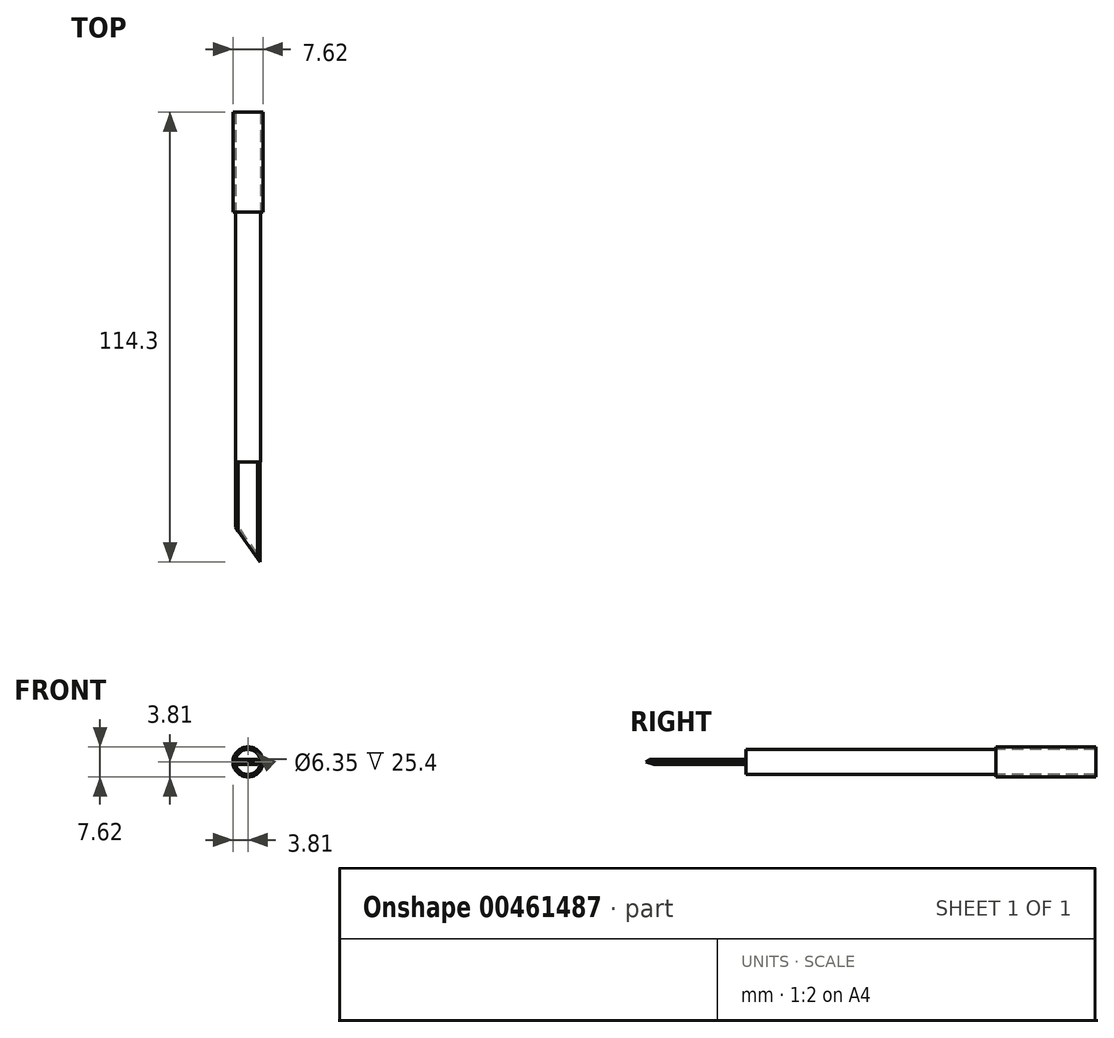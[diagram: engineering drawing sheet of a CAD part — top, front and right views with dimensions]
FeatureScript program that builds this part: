
annotation { "Feature Type Name" : "Feature", "Feature Type Description" : "" }
export const myFeature = defineFeature(function(context is Context, id is Id, definition is map)
    precondition{}
    {
        {
            var Q0;
            Q0=qCreatedBy(makeId("Front.planeOp"),FACE);
            var sketch = newSketch(context, id + "F0", { "sketchPlane" : qUnion([Q0])});
            skCircle(sketch, "E0", {"center": v(0, 0) * mm, "radius": 3.18 * mm});
            skSolve(sketch);
        }
        {
            var Q0;
            Q0=makeQuery(id+"F0.imprint","IMPRINT",FACE,{"disambiguationData":[TD([[makeQuery(id+"F0.imprint","IMPRINT",EDGE,{"derivedFrom":sQuery(id+"F0.wireOp",EDGE,"E0")}),1.0]])]});
            extrude(context, id + "F1", {"entities" : qUnion([Q0]), "depth" : 88.9 * mm});
        }
        {
            var Q0;
            Q0=makeQuery(id+"F1.opExtrude","CAP_FACE",FACE,{"disambiguationData":[OSD([sQuery(id+"F0.wireOp",EDGE,"E0")])],"isStart":false});
            var sketch = newSketch(context, id + "F2", { "sketchPlane" : qUnion([Q0])});
            skLineSegment(sketch, "E1", {"start": v(0, -3.18) * mm, "end": v(0, 0) * mm});
            skLineSegment(sketch, "E2", {"start": v(0, 0) * mm, "end": v(0, 3.18) * mm});
            skLineSegment(sketch, "E3.right", {"start": v(11.11, 0.64) * mm, "end": v(11.11, -0.64) * mm});
            skLineSegment(sketch, "E4", {"start": v(-1.59, 0.64) * mm, "end": v(-3.11, 0.64) * mm});
            skLineSegment(sketch, "E5", {"start": v(-3.11, 0.64) * mm, "end": v(3.11, 0.64) * mm});
            skLineSegment(sketch, "E6", {"start": v(-1.59, -0.64) * mm, "end": v(-3.11, -0.64) * mm});
            skLineSegment(sketch, "E7", {"start": v(-3.11, -0.64) * mm, "end": v(3.11, -0.64) * mm});
            skLineSegment(sketch, "E8.left", {"start": v(-3.11, 0.64) * mm, "end": v(-3.11, -0.64) * mm});
            skLineSegment(sketch, "E8.right", {"start": v(3.11, 0.64) * mm, "end": v(3.11, -0.64) * mm});
            skSolve(sketch);
        }
        {
            var Q0;
            {var subQ4=sQuery(id+"F2.wireOp",EDGE,"E8.left");Q0=makeQuery(id+"F2.imprint","IMPRINT",FACE,{"disambiguationData":[TD([[makeQuery(id+"F2.imprint","IMPRINT",EDGE,{"derivedFrom":subQ4}),1.0]])]});}
            var Q1;
            {var subQ0=sQuery(id+"F2.wireOp",EDGE,"E8.right");Q1=makeQuery(id+"F2.imprint","IMPRINT",FACE,{"disambiguationData":[TD([[makeQuery(id+"F2.imprint","IMPRINT",EDGE,{"derivedFrom":subQ0}),-1.0]])]});}
            extrude(context, id + "F3", {"entities" : qUnion([Q0, Q1]), "operationType" : NewBodyOperationType.ADD, "depth" : 25.4 * mm});
        }
        {
            var Q0;
            Q0=makeQuery(id+"F3.opExtrude","SWEPT_FACE",FACE,{"disambiguationData":[OSD([sQuery(id+"F2.wireOp",EDGE,"E5")])]});
            var sketch = newSketch(context, id + "F4", { "sketchPlane" : qUnion([Q0])});
            skLineSegment(sketch, "E9", {"start": v(3.11, -114.3) * mm, "end": v(-3.11, -105.48) * mm});
            skLineSegment(sketch, "E10", {"start": v(-3.11, -114.3) * mm, "end": v(3.11, -114.3) * mm});
            skSolve(sketch);
        }
        {
            var Q0;
            {var subQ0=sQuery(id+"F4.wireOp",EDGE,"E9");Q0=makeQuery(id+"F4.imprint","IMPRINT",FACE,{"disambiguationData":[TD([[makeQuery(id+"F4.imprint","IMPRINT",EDGE,{"derivedFrom":subQ0}),1.0]])]});}
            extrude(context, id + "F5", {"entities" : qUnion([Q0]), "operationType" : NewBodyOperationType.REMOVE, "oppositeDirection" : true, "depth" : 25.4 * mm});
        }
        {
            var Q0;
            Q0=makeQuery(id+"F3.opExtrude","SWEPT_EDGE",EDGE,{"disambiguationData":[OSD([sQuery(id+"F0.wireOp",EDGE,"E0"),sQuery(id+"F2.wireOp",EDGE,"E5"),sQuery(id+"F2.wireOp",EDGE,"E8.left")])]});
            var Q1;
            Q1=makeQuery(id+"F5.boolean.opBoolean","COPY",EDGE,{"derivedFrom":makeQuery(id+"F5.opExtrude","CAP_EDGE",EDGE,{"disambiguationData":[OSD([sQuery(id+"F4.wireOp",EDGE,"E9")])],"isStart":true})});
            var Q2;
            Q2=makeQuery(id+"F3.opExtrude","SWEPT_EDGE",EDGE,{"disambiguationData":[OSD([sQuery(id+"F0.wireOp",EDGE,"E0"),sQuery(id+"F2.wireOp",EDGE,"E5"),sQuery(id+"F2.wireOp",EDGE,"E8.right")])]});
            chamfer(context, id + "F6", {"entities" : qUnion([Q0, Q1, Q2]), "width" : 0.64 * mm, "tangentPropagation" : true});
        }
        {
            var Q0;
            Q0=makeQuery(id+"F5.boolean.opBoolean","INTERSECT",EDGE,{"derivedFrom":[makeQuery(id+"F3.opExtrude","SWEPT_FACE",FACE,{"disambiguationData":[OSD([sQuery(id+"F2.wireOp",EDGE,"E7")])]}),makeQuery(id+"F5.opExtrude","SWEPT_FACE",FACE,{"disambiguationData":[OSD([sQuery(id+"F4.wireOp",EDGE,"E9")])]})]});
            var Q1;
            Q1=makeQuery(id+"F3.opExtrude","SWEPT_EDGE",EDGE,{"disambiguationData":[OSD([sQuery(id+"F0.wireOp",EDGE,"E0"),sQuery(id+"F2.wireOp",EDGE,"E7"),sQuery(id+"F2.wireOp",EDGE,"E8.left")])]});
            var Q2;
            Q2=makeQuery(id+"F3.opExtrude","SWEPT_EDGE",EDGE,{"disambiguationData":[OSD([sQuery(id+"F0.wireOp",EDGE,"E0"),sQuery(id+"F2.wireOp",EDGE,"E7"),sQuery(id+"F2.wireOp",EDGE,"E8.right")])]});
            chamfer(context, id + "F7", {"entities" : qUnion([Q0, Q1, Q2]), "width" : 0.64 * mm, "tangentPropagation" : true});
        }
        {
            var Q0;
            Q0=makeQuery(id+"F1.opExtrude","CAP_FACE",FACE,{"disambiguationData":[OSD([sQuery(id+"F0.wireOp",EDGE,"E0")])],"isStart":true});
            extrude(context, id + "F8", {"entities" : qUnion([Q0]), "operationType" : NewBodyOperationType.REMOVE, "oppositeDirection" : true, "depth" : 25.4 * mm});
        }
        {
            var Q0;
            Q0=makeQuery(id+"F8.boolean.opBoolean","COPY",FACE,{"derivedFrom":makeQuery(id+"F8.opExtrude","CAP_FACE",FACE,{"disambiguationData":[OSD([sQuery(id+"F0.wireOp",EDGE,"E0")])],"isStart":false})});
            var sketch = newSketch(context, id + "F9", { "sketchPlane" : qUnion([Q0])});
            skCircle(sketch, "E11", {"center": v(0, 0) * mm, "radius": 3.81 * mm});
            skSolve(sketch);
        }
        {
            var Q0;
            Q0=makeQuery(id+"F9.imprint","IMPRINT",FACE,{"disambiguationData":[TD([[makeQuery(id+"F9.imprint","IMPRINT",EDGE,{"derivedFrom":sQuery(id+"F9.wireOp",EDGE,"E11")}),1.0]])]});
            var Q1;
            Q1=makeQuery(id+"F9.imprint","IMPRINT",FACE,{"disambiguationData":[TD([[makeQuery(id+"F9.imprint","IMPRINT",EDGE,{"derivedFrom":makeQuery(id+"F8.boolean.opBoolean","COPY",EDGE,{"derivedFrom":makeQuery(id+"F8.opExtrude","CAP_EDGE",EDGE,{"disambiguationData":[OSD([sQuery(id+"F0.wireOp",EDGE,"E0")])],"isStart":false})})}),-1.0]])]});
            extrude(context, id + "F10", {"entities" : qUnion([Q0, Q1]), "depth" : 25.4 * mm});
        }
    });
